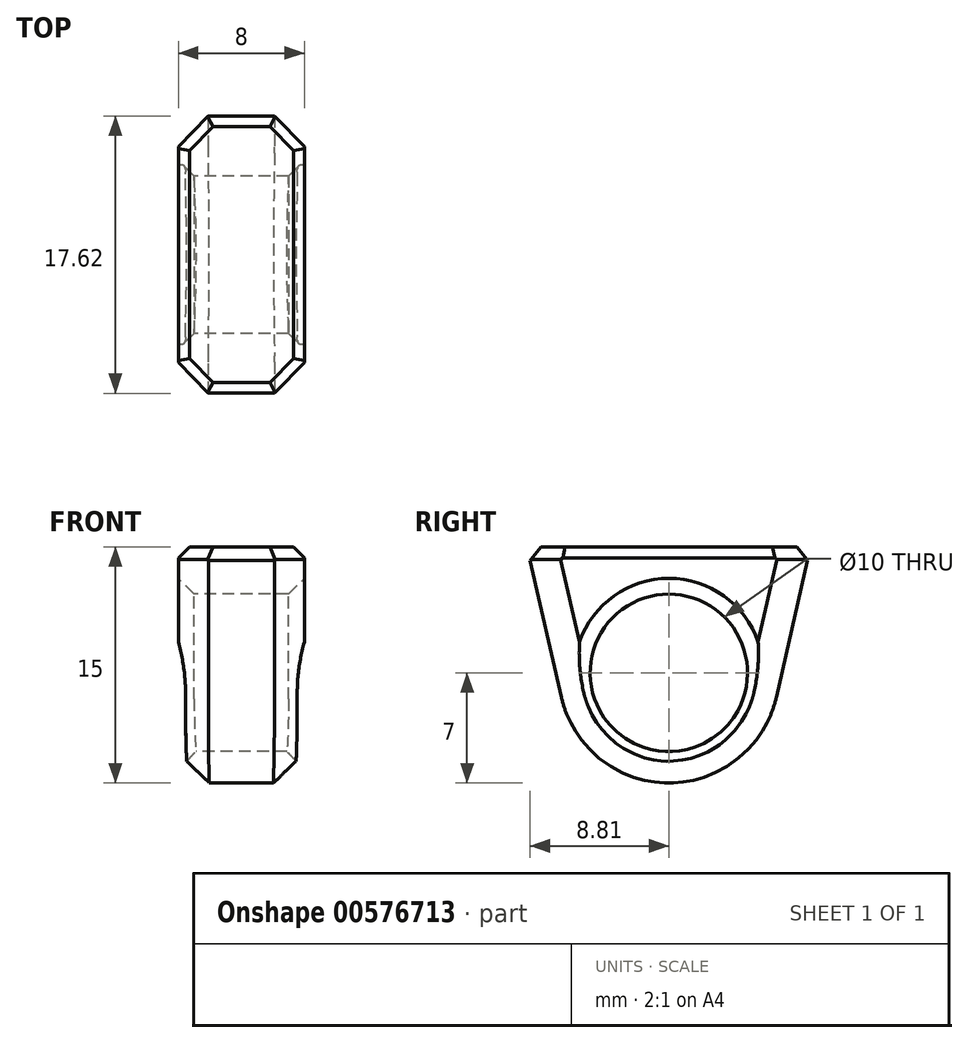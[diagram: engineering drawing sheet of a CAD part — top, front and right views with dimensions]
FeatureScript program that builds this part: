
annotation { "Feature Type Name" : "Feature", "Feature Type Description" : "" }
export const myFeature = defineFeature(function(context is Context, id is Id, definition is map)
    precondition{}
    {
        {
            var Q0;
            Q0=qCreatedBy(makeId("Right.planeOp"),FACE);
            var sketch = newSketch(context, id + "F0", { "sketchPlane" : qUnion([Q0])});
            skCircle(sketch, "E0", {"center": v(0, 0) * mm, "radius": 5 * mm});
            skCircle(sketch, "E1", {"center": v(0, 0) * mm, "radius": 7 * mm});
            skLineSegment(sketch, "E2", {"start": v(9, 8) * mm, "end": v(-9, 8) * mm});
            skLineSegment(sketch, "E3", {"start": v(-9, 8) * mm, "end": v(-6.83, -1.55) * mm});
            skLineSegment(sketch, "E4", {"start": v(9, 8) * mm, "end": v(6.83, -1.55) * mm});
            skPoint(sketch, "E5", {"position": v(0, 8) * mm});
            skSolve(sketch);
        }
        {
            var Q0;
            Q0=qSketchRegion(id+"F0",true);
            extrude(context, id + "F1", {"entities" : qUnion([Q0]), "endBound" : BoundingType.SYMMETRIC, "depth" : 8 * mm});
        }
        {
            var Q0;
            Q0=qCreatedBy(makeId("Front.planeOp"),FACE);
            var sketch = newSketch(context, id + "F2", { "sketchPlane" : qUnion([Q0])});
            skLineSegment(sketch, "E6", {"start": v(4, -2) * mm, "end": v(4, 8) * mm});
            skLineSegment(sketch, "E7", {"start": v(4, 8) * mm, "end": v(9, 8) * mm});
            skLineSegment(sketch, "E8", {"start": v(9, 8) * mm, "end": v(9, -22) * mm});
            skLineSegment(sketch, "E9", {"start": v(9, -22) * mm, "end": v(-9, -22) * mm});
            skLineSegment(sketch, "E10", {"start": v(-9, -22) * mm, "end": v(-9, 8) * mm});
            skLineSegment(sketch, "E11", {"start": v(-9, 8) * mm, "end": v(-4, 8) * mm});
            skLineSegment(sketch, "E12", {"start": v(-4, 8) * mm, "end": v(-4, -2) * mm});
            skArc(sketch, "E13", {"start": v(2.5, -17) * mm, "mid": v(3.62, -9.54) * mm, "end": v(4, -2) * mm});
            skArc(sketch, "E14", {"start": v(-4, -2) * mm, "mid": v(-3.62, -9.54) * mm, "end": v(-2.5, -17) * mm});
            skLineSegment(sketch, "E15", {"start": v(2.5, -17) * mm, "end": v(-2.5, -17) * mm});
            skPoint(sketch, "E16", {"position": v(0, -17) * mm});
            skSolve(sketch);
        }
        {
            var Q0;
            Q0=qSketchRegion(id+"F2",true);
            extrude(context, id + "F3", {"entities" : qUnion([Q0]), "operationType" : NewBodyOperationType.REMOVE, "endBound" : BoundingType.SYMMETRIC, "oppositeDirection" : true, "depth" : 30 * mm});
        }
        {
            var Q0;
            {var subQ0=sQuery(id+"F0.wireOp",EDGE,"E3");var subQ1=sQuery(id+"F0.wireOp",EDGE,"E2");Q0=makeQuery(id+"F3.boolean.opBoolean","SPLIT",EDGE,{"disambiguationData":[TD([makeQuery(id+"F1.opExtrude","SWEPT_FACE",FACE,{"disambiguationData":[OSD([subQ1])]})])],"derivedFrom":makeQuery(id+"F1.opExtrude","CAP_EDGE",EDGE,{"disambiguationData":[OSD([subQ0])],"isStart":true})});}
            var Q1;
            {var subQ0=sQuery(id+"F0.wireOp",EDGE,"E4");var subQ1=sQuery(id+"F0.wireOp",EDGE,"E2");Q1=makeQuery(id+"F3.boolean.opBoolean","SPLIT",EDGE,{"disambiguationData":[TD([makeQuery(id+"F1.opExtrude","SWEPT_FACE",FACE,{"disambiguationData":[OSD([subQ1])]})])],"derivedFrom":makeQuery(id+"F1.opExtrude","CAP_EDGE",EDGE,{"disambiguationData":[OSD([subQ0])],"isStart":false})});}
            chamfer(context, id + "F4", {"entities" : qUnion([Q0, Q1]), "width" : 1.9 * mm, "tangentPropagation" : true});
        }
        {
            var Q0;
            Q0=makeQuery(id+"F1.opExtrude","CAP_EDGE",EDGE,{"disambiguationData":[OSD([sQuery(id+"F0.wireOp",EDGE,"E0")])],"isStart":true});
            var Q1;
            Q1=makeQuery(id+"F1.opExtrude","CAP_EDGE",EDGE,{"disambiguationData":[OSD([sQuery(id+"F0.wireOp",EDGE,"E0")])],"isStart":false});
            chamfer(context, id + "F5", {"entities" : qUnion([Q0, Q1]), "width" : 1 * mm, "tangentPropagation" : true});
        }
        {
            var Q0;
            Q0=makeQuery(id+"F1.opExtrude","CAP_EDGE",EDGE,{"disambiguationData":[OSD([sQuery(id+"F0.wireOp",EDGE,"E2")])],"isStart":true});
            var Q1;
            {var subQ0=sQuery(id+"F0.wireOp",EDGE,"E4");var subQ1=sQuery(id+"F0.wireOp",EDGE,"E2");var subQ2=makeQuery(id+"F1.opExtrude","SWEPT_FACE",FACE,{"disambiguationData":[OSD([subQ1])]});Q1=makeQuery(id+"F4.opChamfer","BLEND_EDGE",EDGE,{"blendedFrom":[makeQuery(id+"F3.boolean.opBoolean","SPLIT",EDGE,{"disambiguationData":[TD([subQ2])],"derivedFrom":makeQuery(id+"F1.opExtrude","CAP_EDGE",EDGE,{"disambiguationData":[OSD([subQ0])],"isStart":true})}),subQ2],"blendedInto":[subQ2]});}
            var Q2;
            Q2=makeQuery(id+"F1.opExtrude","SWEPT_EDGE",EDGE,{"disambiguationData":[OSD([sQuery(id+"F0.wireOp",EDGE,"E2"),sQuery(id+"F0.wireOp",EDGE,"E4")])]});
            var Q3;
            {var subQ0=sQuery(id+"F0.wireOp",EDGE,"E4");var subQ1=sQuery(id+"F0.wireOp",EDGE,"E2");var subQ2=makeQuery(id+"F1.opExtrude","SWEPT_FACE",FACE,{"disambiguationData":[OSD([subQ1])]});Q3=makeQuery(id+"F4.opChamfer","BLEND_EDGE",EDGE,{"blendedFrom":[makeQuery(id+"F3.boolean.opBoolean","SPLIT",EDGE,{"disambiguationData":[TD([subQ2])],"derivedFrom":makeQuery(id+"F1.opExtrude","CAP_EDGE",EDGE,{"disambiguationData":[OSD([subQ0])],"isStart":false})}),subQ2],"blendedInto":[subQ2]});}
            var Q4;
            Q4=makeQuery(id+"F1.opExtrude","CAP_EDGE",EDGE,{"disambiguationData":[OSD([sQuery(id+"F0.wireOp",EDGE,"E2")])],"isStart":false});
            var Q5;
            {var subQ0=sQuery(id+"F0.wireOp",EDGE,"E3");var subQ1=sQuery(id+"F0.wireOp",EDGE,"E2");var subQ2=makeQuery(id+"F1.opExtrude","SWEPT_FACE",FACE,{"disambiguationData":[OSD([subQ1])]});Q5=makeQuery(id+"F4.opChamfer","BLEND_EDGE",EDGE,{"blendedFrom":[makeQuery(id+"F3.boolean.opBoolean","SPLIT",EDGE,{"disambiguationData":[TD([subQ2])],"derivedFrom":makeQuery(id+"F1.opExtrude","CAP_EDGE",EDGE,{"disambiguationData":[OSD([subQ0])],"isStart":false})}),subQ2],"blendedInto":[subQ2]});}
            var Q6;
            Q6=makeQuery(id+"F1.opExtrude","SWEPT_EDGE",EDGE,{"disambiguationData":[OSD([sQuery(id+"F0.wireOp",EDGE,"E2"),sQuery(id+"F0.wireOp",EDGE,"E3")])]});
            var Q7;
            {var subQ0=sQuery(id+"F0.wireOp",EDGE,"E3");var subQ1=sQuery(id+"F0.wireOp",EDGE,"E2");var subQ2=makeQuery(id+"F1.opExtrude","SWEPT_FACE",FACE,{"disambiguationData":[OSD([subQ1])]});Q7=makeQuery(id+"F4.opChamfer","BLEND_EDGE",EDGE,{"blendedFrom":[makeQuery(id+"F3.boolean.opBoolean","SPLIT",EDGE,{"disambiguationData":[TD([subQ2])],"derivedFrom":makeQuery(id+"F1.opExtrude","CAP_EDGE",EDGE,{"disambiguationData":[OSD([subQ0])],"isStart":true})}),subQ2],"blendedInto":[subQ2]});}
            chamfer(context, id + "F6", {"entities" : qUnion([Q0, Q1, Q2, Q3, Q4, Q5, Q6, Q7]), "width" : 0.7 * mm, "tangentPropagation" : true});
        }
    });
